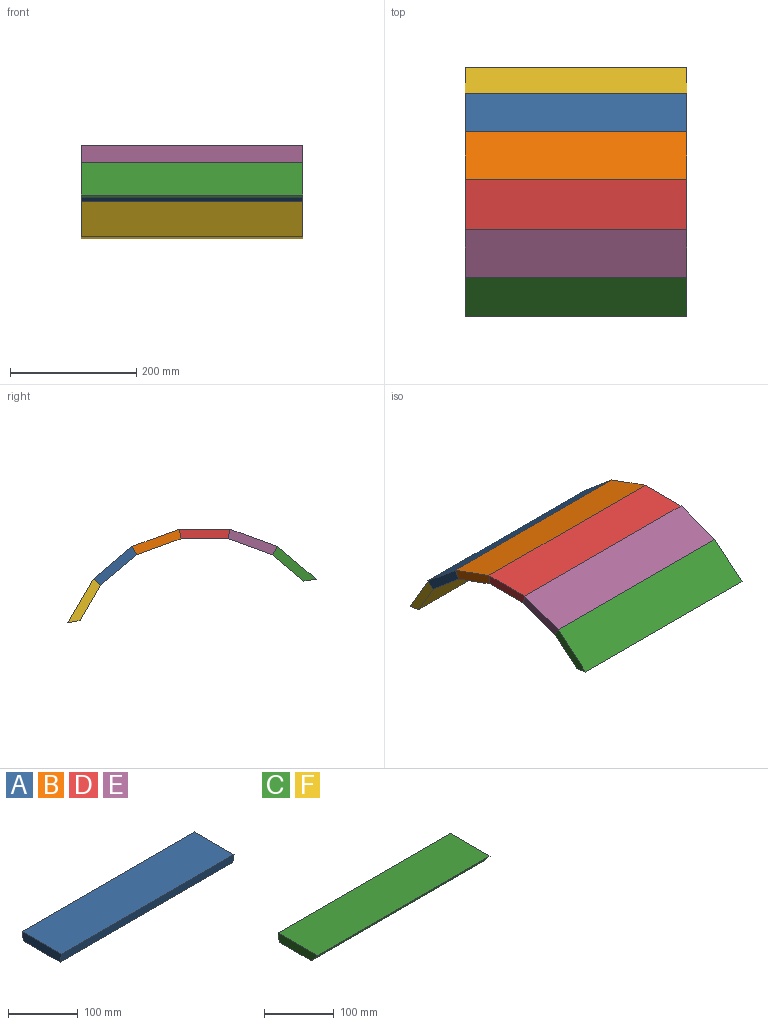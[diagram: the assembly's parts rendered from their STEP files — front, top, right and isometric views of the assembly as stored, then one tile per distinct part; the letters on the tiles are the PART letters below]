
ASSEMBLY  parts=6 mates=5
PART A: 6 faces, bbox 350x80x15 mm
  f0: plane 350x80mm, normal (0,0,1), area 28000mm2, adj f1,f3,f4,f5
  f1: plane 350x15mm, normal (0,-0.98,-0.17), area 5331mm2, adj f0,f2,f4,f5
  f2: plane 350x74.71mm, normal (0,0,-1), area 26148.6mm2, adj f1,f3,f4,f5
  f3: plane 350x15mm, normal (0,0.98,-0.17), area 5331mm2, adj f0,f2,f4,f5
  f4: plane 80x15mm, normal (1,0,0), area 1160.3mm2, adj f0,f1,f2,f3
  f5: plane 80x15mm, normal (-1,0,0), area 1160.3mm2, adj f0,f1,f2,f3
PART B: same geometry as A
PART C: 6 faces, bbox 350x80x15 mm
  f0: plane 350x80mm, normal (0,0,1), area 28000mm2, adj f1,f3,f4,f5
  f1: plane 350x15mm, normal (0,-0.77,-0.64), area 6853.4mm2, adj f0,f2,f4,f5
  f2: plane 350x64.77mm, normal (0,0,-1), area 22669mm2, adj f1,f3,f4,f5
  f3: plane 350x15mm, normal (0,0.98,-0.17), area 5331mm2, adj f0,f2,f4,f5
  f4: plane 80x15mm, normal (1,0,0), area 1085.8mm2, adj f0,f1,f2,f3
  f5: plane 80x15mm, normal (-1,0,0), area 1085.8mm2, adj f0,f1,f2,f3
PART D: same geometry as A
PART E: same geometry as A
PART F: same geometry as C
PLACE A rot(axis=(-1,0,0),40deg) t=(-175,222.87,92.62)mm
PLACE B rot(axis=(-1,0,0),20deg) t=(-175,147.69,119.98)mm
PLACE C rot(axis=(1,0,0),40deg) t=(-175,-68.77,41.2)mm
PLACE D t=(-175,67.69,119.98)mm
PLACE E rot(axis=(1,0,0),20deg) t=(-175,-7.48,92.62)mm
PLACE F rot(axis=(0,0.5,0.87),180deg) t=(175,324.15,-28.09)mm
MATE slider A.f1 <-> B.f3  axis (0,-0.87,0.5) through (175,215.25,79.43)mm
MATE slider F.f3 <-> A.f3  axis (0,-0.64,0.77) through (175,272.48,31.41)mm
MATE slider C.f3 <-> E.f1  axis (0,0.87,0.5) through (175,0.13,79.43)mm
MATE slider B.f1 <-> D.f3  axis (0,-0.98,0.17) through (175,145.05,104.98)mm
MATE revolute E.f3 <-> D.f1  axis (0,0.98,0.17) through (175,70.34,104.98)mm
